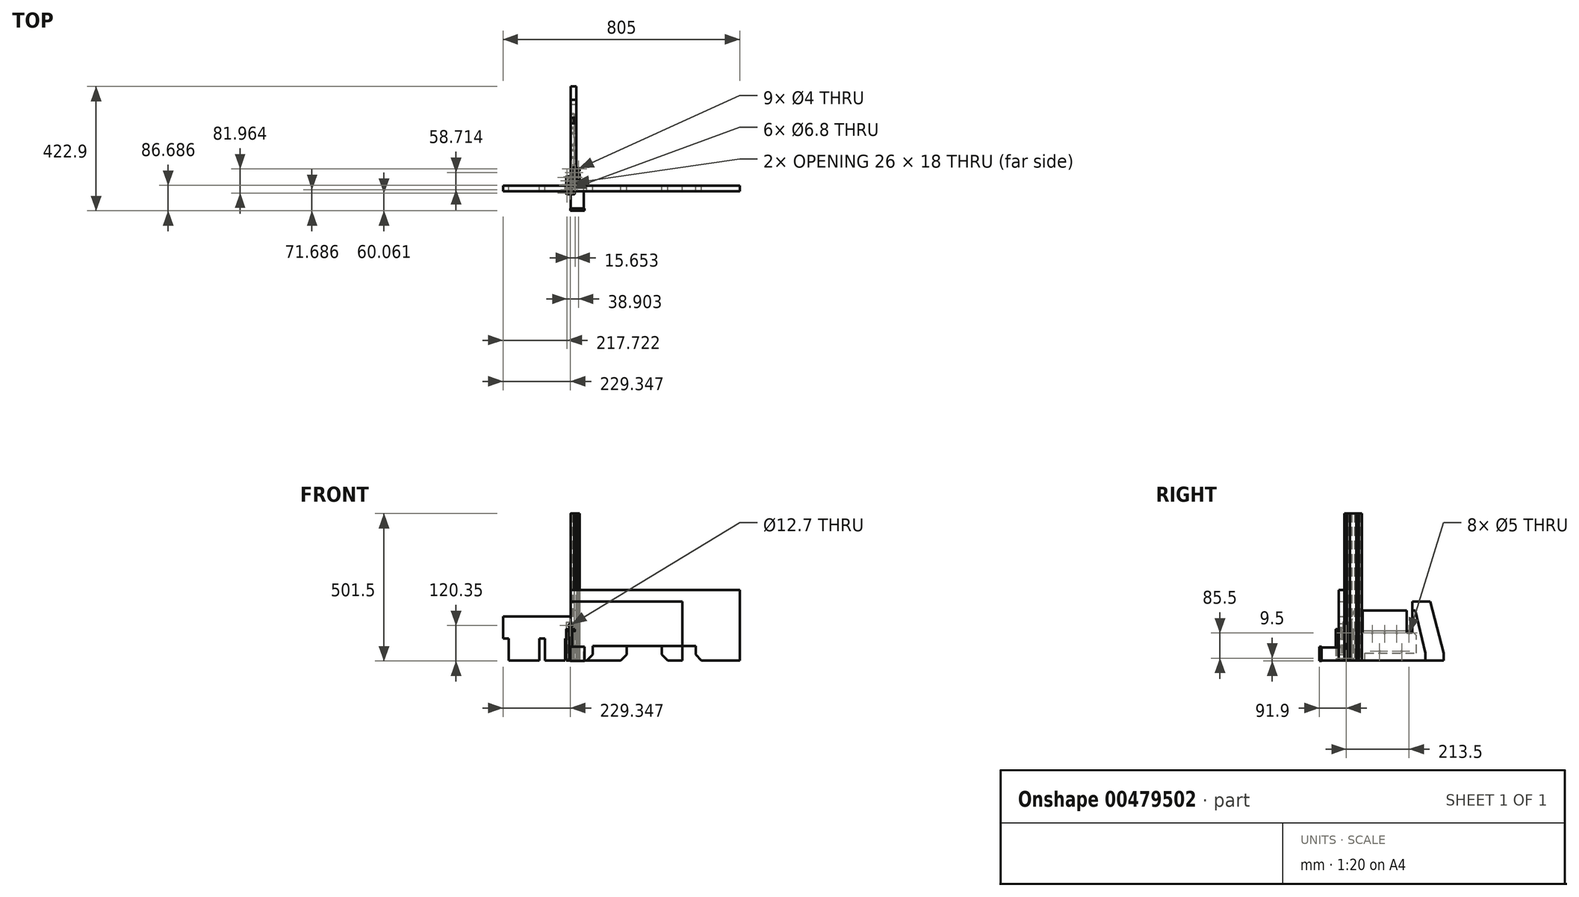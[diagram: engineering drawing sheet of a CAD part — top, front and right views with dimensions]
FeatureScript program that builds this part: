
annotation { "Feature Type Name" : "Feature", "Feature Type Description" : "" }
export const myFeature = defineFeature(function(context is Context, id is Id, definition is map)
    precondition{}
    {
        {
            var Q0;
            Q0=qCreatedBy(makeId("Top.planeOp"),FACE);
            var sketch = newSketch(context, id + "F0", { "sketchPlane" : qUnion([Q0])});
            skLineSegment(sketch, "E0.bottom", {"start": v(2, 60) * mm, "end": v(28, 60) * mm});
            skLineSegment(sketch, "E0.top", {"start": v(2, 0) * mm, "end": v(28, 0) * mm});
            skLineSegment(sketch, "E0.left", {"start": v(0, 58) * mm, "end": v(0, 2) * mm});
            skLineSegment(sketch, "E0.right", {"start": v(30, 58) * mm, "end": v(30, 2) * mm});
            skCircle(sketch, "E1", {"center": v(3.37, 56.62) * mm, "radius": 2 * mm});
            skCircle(sketch, "E2", {"center": v(26.62, 56.62) * mm, "radius": 2 * mm});
            skCircle(sketch, "E3", {"center": v(26.62, 3.38) * mm, "radius": 2 * mm});
            skCircle(sketch, "E4", {"center": v(3.37, 3.37) * mm, "radius": 2 * mm});
            skCircle(sketch, "E5", {"center": v(15, 45) * mm, "radius": 3.4 * mm});
            skCircle(sketch, "E6", {"center": v(15, 15) * mm, "radius": 3.4 * mm});
            skLineSegment(sketch, "E7", {"start": v(15, 60) * mm, "end": v(15, 0) * mm, "construction": true});
            skLineSegment(sketch, "E8.bottom", {"start": v(21, 39) * mm, "end": v(9, 39) * mm});
            skLineSegment(sketch, "E8.top", {"start": v(21, 51) * mm, "end": v(10.41, 51) * mm});
            skLineSegment(sketch, "E8.left", {"start": v(21, 39) * mm, "end": v(21, 51) * mm});
            skLineSegment(sketch, "E8.right", {"start": v(9, 39) * mm, "end": v(9, 49.59) * mm});
            skPoint(sketch, "E9.visualSharp", {"position": v(30, 60) * mm});
            skArc(sketch, "E9.filletArc", {"start": v(30, 58) * mm, "mid": v(29.41, 59.41) * mm, "end": v(28, 60) * mm});
            skPoint(sketch, "E10.visualSharp", {"position": v(0, 60) * mm});
            skArc(sketch, "E10.filletArc", {"start": v(2, 60) * mm, "mid": v(0.59, 59.41) * mm, "end": v(0, 58) * mm});
            skPoint(sketch, "E11.visualSharp", {"position": v(0, 0) * mm});
            skArc(sketch, "E11.filletArc", {"start": v(0, 2) * mm, "mid": v(0.59, 0.59) * mm, "end": v(2, 0) * mm});
            skPoint(sketch, "E12.visualSharp", {"position": v(30, 0) * mm});
            skArc(sketch, "E12.filletArc", {"start": v(28, 0) * mm, "mid": v(29.41, 0.59) * mm, "end": v(30, 2) * mm});
            skLineSegment(sketch, "E13.bottom", {"start": v(21, 9) * mm, "end": v(9, 9) * mm});
            skLineSegment(sketch, "E13.top", {"start": v(21, 21) * mm, "end": v(9, 21) * mm});
            skLineSegment(sketch, "E13.left", {"start": v(21, 9) * mm, "end": v(21, 21) * mm});
            skLineSegment(sketch, "E13.right", {"start": v(9, 9) * mm, "end": v(9, 21) * mm});
            skLineSegment(sketch, "E14", {"start": v(0, 49) * mm, "end": v(2, 49) * mm});
            skLineSegment(sketch, "E15", {"start": v(2, 49) * mm, "end": v(2, 53.38) * mm});
            skLineSegment(sketch, "E16", {"start": v(2, 53.37) * mm, "end": v(5.21, 53.37) * mm});
            skLineSegment(sketch, "E17", {"start": v(5.21, 53.38) * mm, "end": v(9, 49.59) * mm});
            skLineSegment(sketch, "E18", {"start": v(11, 60) * mm, "end": v(11, 58) * mm});
            skLineSegment(sketch, "E19", {"start": v(11, 58) * mm, "end": v(6.62, 58) * mm});
            skLineSegment(sketch, "E20", {"start": v(6.62, 58) * mm, "end": v(6.62, 54.79) * mm});
            skLineSegment(sketch, "E21", {"start": v(6.63, 54.79) * mm, "end": v(10.41, 51) * mm});
            skPoint(sketch, "E22.orphan", {"position": v(9, 51) * mm});
            skLineSegment(sketch, "E23", {"start": v(0, 30) * mm, "end": v(30, 30) * mm, "construction": true});
            skPoint(sketch, "E24.MirrorP", {"position": v(21, 51) * mm});
            skLineSegment(sketch, "E25.MirrorCS", {"start": v(30, 49) * mm, "end": v(28, 49) * mm});
            skLineSegment(sketch, "E26.MirrorCS", {"start": v(24.79, 53.38) * mm, "end": v(21, 49.59) * mm});
            skCircle(sketch, "E27.MirrorC", {"center": v(26.63, 56.62) * mm, "radius": 2 * mm});
            skLineSegment(sketch, "E28.MirrorCS", {"start": v(28, 49) * mm, "end": v(28, 53.38) * mm});
            skLineSegment(sketch, "E29.MirrorCS", {"start": v(19, 58) * mm, "end": v(23.38, 58) * mm});
            skLineSegment(sketch, "E30.MirrorCS", {"start": v(23.37, 54.79) * mm, "end": v(19.59, 51) * mm});
            skLineSegment(sketch, "E31.MirrorCS", {"start": v(19, 60) * mm, "end": v(19, 58) * mm});
            skLineSegment(sketch, "E32.MirrorCS", {"start": v(23.38, 58) * mm, "end": v(23.38, 54.79) * mm});
            skArc(sketch, "E33.MirrorCS", {"start": v(28, 60) * mm, "mid": v(29.41, 59.41) * mm, "end": v(30, 58) * mm});
            skLineSegment(sketch, "E34.MirrorCS", {"start": v(28, 53.37) * mm, "end": v(24.79, 53.37) * mm});
            skArc(sketch, "E35.MirrorCS", {"start": v(30, 2) * mm, "mid": v(29.41, 0.59) * mm, "end": v(28, 0) * mm});
            skCircle(sketch, "E36.MirrorC", {"center": v(26.62, 3.37) * mm, "radius": 2 * mm});
            skCircle(sketch, "E37.MirrorC", {"center": v(26.63, 3.38) * mm, "radius": 2 * mm});
            skLineSegment(sketch, "E38.MirrorCS", {"start": v(19, 0) * mm, "end": v(19, 2) * mm});
            skLineSegment(sketch, "E39.MirrorCS", {"start": v(28, 6.63) * mm, "end": v(24.79, 6.63) * mm});
            skLineSegment(sketch, "E40.MirrorCS", {"start": v(28, 11) * mm, "end": v(28, 6.62) * mm});
            skPoint(sketch, "E41.MirrorP", {"position": v(21, 9) * mm});
            skLineSegment(sketch, "E42.MirrorCS", {"start": v(23.37, 5.21) * mm, "end": v(19.59, 9) * mm});
            skLineSegment(sketch, "E43.MirrorCS", {"start": v(30, 11) * mm, "end": v(28, 11) * mm});
            skLineSegment(sketch, "E44.MirrorCS", {"start": v(19, 2) * mm, "end": v(23.38, 2) * mm});
            skLineSegment(sketch, "E45.MirrorCS", {"start": v(24.79, 6.62) * mm, "end": v(21, 10.41) * mm});
            skLineSegment(sketch, "E46.MirrorCS", {"start": v(23.38, 2) * mm, "end": v(23.38, 5.21) * mm});
            skLineSegment(sketch, "E47.MirrorCS", {"start": v(0, 11) * mm, "end": v(2, 11) * mm});
            skArc(sketch, "E48.MirrorCS", {"start": v(2, 0) * mm, "mid": v(0.59, 0.59) * mm, "end": v(0, 2) * mm});
            skLineSegment(sketch, "E49.MirrorCS", {"start": v(11, 0) * mm, "end": v(11, 2) * mm});
            skLineSegment(sketch, "E50.MirrorCS", {"start": v(2, 6.63) * mm, "end": v(5.21, 6.63) * mm});
            skLineSegment(sketch, "E51.MirrorCS", {"start": v(5.21, 6.62) * mm, "end": v(9, 10.41) * mm});
            skPoint(sketch, "E52.MirrorP", {"position": v(9, 9) * mm});
            skLineSegment(sketch, "E53.MirrorCS", {"start": v(6.63, 5.21) * mm, "end": v(10.41, 9) * mm});
            skCircle(sketch, "E54.MirrorC", {"center": v(3.37, 3.38) * mm, "radius": 2 * mm});
            skLineSegment(sketch, "E55.MirrorCS", {"start": v(11, 2) * mm, "end": v(6.62, 2) * mm});
            skLineSegment(sketch, "E56.MirrorCS", {"start": v(6.62, 2) * mm, "end": v(6.62, 5.21) * mm});
            skLineSegment(sketch, "E57.MirrorCS", {"start": v(2, 11) * mm, "end": v(2, 6.62) * mm});
            skLineSegment(sketch, "E58", {"start": v(9, 51) * mm, "end": v(10.41, 51) * mm});
            skLineSegment(sketch, "E59", {"start": v(9, 49.59) * mm, "end": v(9, 51) * mm});
            skLineSegment(sketch, "E60", {"start": v(0, 41) * mm, "end": v(2, 41) * mm});
            skLineSegment(sketch, "E61", {"start": v(2, 41) * mm, "end": v(2, 36.62) * mm});
            skLineSegment(sketch, "E62", {"start": v(2, 36.62) * mm, "end": v(5.21, 36.62) * mm});
            skLineSegment(sketch, "E63", {"start": v(5.21, 36.62) * mm, "end": v(9, 40.41) * mm});
            skLineSegment(sketch, "E64", {"start": v(10.41, 39) * mm, "end": v(6.04, 34.62) * mm});
            skLineSegment(sketch, "E65", {"start": v(6.04, 34.62) * mm, "end": v(2, 34.62) * mm});
            skLineSegment(sketch, "E66", {"start": v(2, 34.62) * mm, "end": v(2, 30) * mm});
            skLineSegment(sketch, "E67.MirrorCS", {"start": v(30, 41) * mm, "end": v(28, 41) * mm});
            skLineSegment(sketch, "E68.MirrorCS", {"start": v(28, 34.62) * mm, "end": v(28, 30) * mm});
            skLineSegment(sketch, "E69.MirrorCS", {"start": v(28, 41) * mm, "end": v(28, 36.62) * mm});
            skLineSegment(sketch, "E70.MirrorCS", {"start": v(19.59, 39) * mm, "end": v(23.96, 34.62) * mm});
            skLineSegment(sketch, "E71.MirrorCS", {"start": v(23.96, 34.62) * mm, "end": v(28, 34.62) * mm});
            skLineSegment(sketch, "E72.MirrorCS", {"start": v(28, 36.62) * mm, "end": v(24.79, 36.62) * mm});
            skLineSegment(sketch, "E73.MirrorCS", {"start": v(24.79, 36.62) * mm, "end": v(21, 40.41) * mm});
            skLineSegment(sketch, "E74.MirrorCS", {"start": v(28, 23.38) * mm, "end": v(24.79, 23.38) * mm});
            skLineSegment(sketch, "E75.MirrorCS", {"start": v(28, 25.38) * mm, "end": v(28, 30) * mm});
            skLineSegment(sketch, "E76.MirrorCS", {"start": v(19.59, 21) * mm, "end": v(23.96, 25.38) * mm});
            skLineSegment(sketch, "E77.MirrorCS", {"start": v(2, 19) * mm, "end": v(2, 23.38) * mm});
            skLineSegment(sketch, "E78.MirrorCS", {"start": v(28, 19) * mm, "end": v(28, 23.38) * mm});
            skLineSegment(sketch, "E79.MirrorCS", {"start": v(2, 25.38) * mm, "end": v(2, 30) * mm});
            skLineSegment(sketch, "E80.MirrorCS", {"start": v(10.41, 21) * mm, "end": v(6.04, 25.38) * mm});
            skLineSegment(sketch, "E81.MirrorCS", {"start": v(24.79, 23.38) * mm, "end": v(21, 19.59) * mm});
            skLineSegment(sketch, "E82.MirrorCS", {"start": v(2, 23.38) * mm, "end": v(5.21, 23.38) * mm});
            skLineSegment(sketch, "E83.MirrorCS", {"start": v(23.96, 25.38) * mm, "end": v(28, 25.38) * mm});
            skLineSegment(sketch, "E84.MirrorCS", {"start": v(5.21, 23.38) * mm, "end": v(9, 19.59) * mm});
            skLineSegment(sketch, "E85.MirrorCS", {"start": v(30, 19) * mm, "end": v(28, 19) * mm});
            skLineSegment(sketch, "E86.MirrorCS", {"start": v(6.04, 25.38) * mm, "end": v(2, 25.38) * mm});
            skLineSegment(sketch, "E87.MirrorCS", {"start": v(0, 19) * mm, "end": v(2, 19) * mm});
            skSolve(sketch);
        }
        {
            var Q0;
            Q0=makeQuery(id+"F0.imprint","IMPRINT",FACE,{"disambiguationData":[TD([[makeQuery(id+"F0.imprint","IMPRINT",EDGE,{"derivedFrom":sQuery(id+"F0.wireOp",EDGE,"E1")}),-1.0]])]});
            var Q1;
            {var subQ5=sQuery(id+"F0.wireOp",EDGE,"E25.MirrorCS");Q1=makeQuery(id+"F0.imprint","IMPRINT",FACE,{"disambiguationData":[TD([[makeQuery(id+"F0.imprint","IMPRINT",EDGE,{"derivedFrom":subQ5}),-1.0]])]});}
            var Q2;
            Q2=makeQuery(id+"F0.imprint","IMPRINT",FACE,{"disambiguationData":[TD([[makeQuery(id+"F0.imprint","IMPRINT",EDGE,{"derivedFrom":sQuery(id+"F0.wireOp",EDGE,"E5")}),-1.0]])]});
            var Q3;
            {var subQ4=sQuery(id+"F0.wireOp",EDGE,"E67.MirrorCS");Q3=makeQuery(id+"F0.imprint","IMPRINT",FACE,{"disambiguationData":[TD([[makeQuery(id+"F0.imprint","IMPRINT",EDGE,{"derivedFrom":subQ4}),1.0]])]});}
            var Q4;
            {var subQ6=sQuery(id+"F0.wireOp",EDGE,"E60");Q4=makeQuery(id+"F0.imprint","IMPRINT",FACE,{"disambiguationData":[TD([[makeQuery(id+"F0.imprint","IMPRINT",EDGE,{"derivedFrom":subQ6}),-1.0]])]});}
            var Q5;
            Q5=makeQuery(id+"F0.imprint","IMPRINT",FACE,{"disambiguationData":[TD([[makeQuery(id+"F0.imprint","IMPRINT",EDGE,{"derivedFrom":sQuery(id+"F0.wireOp",EDGE,"E6")}),-1.0]])]});
            var Q6;
            {var subQ5=sQuery(id+"F0.wireOp",EDGE,"E47.MirrorCS");Q6=makeQuery(id+"F0.imprint","IMPRINT",FACE,{"disambiguationData":[TD([[makeQuery(id+"F0.imprint","IMPRINT",EDGE,{"derivedFrom":subQ5}),-1.0]])]});}
            var Q7;
            {var subQ1=sQuery(id+"F0.wireOp",EDGE,"E12.filletArc");Q7=makeQuery(id+"F0.imprint","IMPRINT",FACE,{"disambiguationData":[TD([[makeQuery(id+"F0.imprint","IMPRINT",EDGE,{"derivedFrom":subQ1}),1.0]])]});}
            extrude(context, id + "F1", {"entities" : qUnion([Q0, Q1, Q2, Q3, Q4, Q5, Q6, Q7]), "depth" : 500 * mm});
        }
        {
            var Q0;
            Q0=qCreatedBy(makeId("Front.planeOp"),FACE);
            var sketch = newSketch(context, id + "F2", { "sketchPlane" : qUnion([Q0])});
            skLineSegment(sketch, "E88.bottom", {"start": v(0, 0) * mm, "end": v(-230, 0) * mm});
            skLineSegment(sketch, "E88.top", {"start": v(0, 150) * mm, "end": v(-230, 150) * mm});
            skLineSegment(sketch, "E88.left", {"start": v(0, 0) * mm, "end": v(0, 150) * mm});
            skLineSegment(sketch, "E88.right", {"start": v(-230, 0) * mm, "end": v(-230, 150) * mm});
            skLineSegment(sketch, "E89", {"start": v(-106, 75) * mm, "end": v(-106, 0) * mm});
            skLineSegment(sketch, "E90", {"start": v(-87, 75) * mm, "end": v(-87, 0) * mm});
            skLineSegment(sketch, "E91", {"start": v(-106, 75) * mm, "end": v(-87, 75) * mm});
            skLineSegment(sketch, "E92", {"start": v(-230, 75) * mm, "end": v(-211, 75) * mm});
            skLineSegment(sketch, "E93", {"start": v(-211, 75) * mm, "end": v(-211, 0) * mm});
            skLineSegment(sketch, "E94", {"start": v(0, 75) * mm, "end": v(-19, 75) * mm});
            skLineSegment(sketch, "E95", {"start": v(-19, 75) * mm, "end": v(-19, 0) * mm});
            skSolve(sketch);
        }
        {
            var Q0;
            {var subQ4=sQuery(id+"F2.wireOp",EDGE,"E88.top");Q0=makeQuery(id+"F2.imprint","IMPRINT",FACE,{"disambiguationData":[TD([[makeQuery(id+"F2.imprint","IMPRINT",EDGE,{"derivedFrom":subQ4}),1.0]])]});}
            extrude(context, id + "F3", {"entities" : qUnion([Q0]), "depth" : 19 * mm});
        }
        {
            var Q0;
            Q0=qCreatedBy(makeId("Right.planeOp"),FACE);
            var sketch = newSketch(context, id + "F4", { "sketchPlane" : qUnion([Q0])});
            skLineSegment(sketch, "E96", {"start": v(0, 0) * mm, "end": v(275, 0) * mm});
            skLineSegment(sketch, "E97", {"start": v(241.5, 170) * mm, "end": v(231.5, 170) * mm});
            skLineSegment(sketch, "E98", {"start": v(231.5, 170) * mm, "end": v(231.5, 95) * mm});
            skLineSegment(sketch, "E99", {"start": v(231.5, 95) * mm, "end": v(212.5, 95) * mm});
            skLineSegment(sketch, "E100", {"start": v(212.5, 95) * mm, "end": v(212.5, 170) * mm});
            skLineSegment(sketch, "E101", {"start": v(212.5, 170) * mm, "end": v(62.5, 170) * mm});
            skLineSegment(sketch, "E102", {"start": v(62.5, 170) * mm, "end": v(62.5, 95) * mm});
            skLineSegment(sketch, "E103", {"start": v(62.5, 95) * mm, "end": v(43.5, 95) * mm});
            skLineSegment(sketch, "E104", {"start": v(43.5, 95) * mm, "end": v(43.5, 170) * mm});
            skLineSegment(sketch, "E105", {"start": v(43.5, 170) * mm, "end": v(33.5, 170) * mm});
            skLineSegment(sketch, "E106", {"start": v(275, 0) * mm, "end": v(275, 25) * mm});
            skLineSegment(sketch, "E107", {"start": v(275, 25) * mm, "end": v(241.5, 170) * mm});
            skLineSegment(sketch, "E108", {"start": v(0, 0) * mm, "end": v(0, 25) * mm});
            skLineSegment(sketch, "E109", {"start": v(0, 25) * mm, "end": v(33.5, 170) * mm});
            skSolve(sketch);
        }
        {
            var Q0;
            Q0=makeQuery(id+"F4.imprint","IMPRINT",FACE,{"disambiguationData":[TD([[makeQuery(id+"F4.imprint","IMPRINT",EDGE,{"derivedFrom":sQuery(id+"F4.wireOp",EDGE,"E96")}),1.0]])]});
            extrude(context, id + "F5", {"entities" : qUnion([Q0]), "depth" : 19 * mm});
        }
        {
            var Q0;
            Q0=qCreatedBy(makeId("Top.planeOp"),FACE);
            var sketch = newSketch(context, id + "F6", { "sketchPlane" : qUnion([Q0])});
            skLineSegment(sketch, "E110.bottom", {"start": v(-13.65, 31.29) * mm, "end": v(12.35, 31.29) * mm});
            skLineSegment(sketch, "E110.top", {"start": v(-13.65, -28.71) * mm, "end": v(12.35, -28.71) * mm});
            skLineSegment(sketch, "E110.left", {"start": v(-15.65, 29.29) * mm, "end": v(-15.65, -26.71) * mm});
            skLineSegment(sketch, "E110.right", {"start": v(14.35, 29.29) * mm, "end": v(14.35, -26.71) * mm});
            skCircle(sketch, "E111", {"center": v(-12.28, 27.91) * mm, "radius": 2 * mm});
            skCircle(sketch, "E112", {"center": v(10.97, 27.91) * mm, "radius": 2 * mm});
            skCircle(sketch, "E113", {"center": v(10.97, -25.34) * mm, "radius": 2 * mm});
            skCircle(sketch, "E114", {"center": v(-12.28, -25.34) * mm, "radius": 2 * mm});
            skCircle(sketch, "E115", {"center": v(-0.65, 16.29) * mm, "radius": 3.4 * mm});
            skCircle(sketch, "E116", {"center": v(-0.65, -13.71) * mm, "radius": 3.4 * mm});
            skLineSegment(sketch, "E117", {"start": v(-0.65, 31.29) * mm, "end": v(-0.65, -28.71) * mm, "construction": true});
            skLineSegment(sketch, "E118.bottom", {"start": v(5.35, 10.29) * mm, "end": v(-6.65, 10.29) * mm});
            skLineSegment(sketch, "E118.top", {"start": v(5.35, 22.29) * mm, "end": v(-5.24, 22.29) * mm});
            skLineSegment(sketch, "E118.left", {"start": v(5.35, 10.29) * mm, "end": v(5.35, 22.29) * mm});
            skLineSegment(sketch, "E118.right", {"start": v(-6.65, 10.29) * mm, "end": v(-6.65, 20.87) * mm});
            skPoint(sketch, "E119.visualSharp", {"position": v(14.35, 31.29) * mm});
            skArc(sketch, "E119.filletArc", {"start": v(14.35, 29.29) * mm, "mid": v(13.76, 30.7) * mm, "end": v(12.35, 31.29) * mm});
            skPoint(sketch, "E120.visualSharp", {"position": v(-15.65, 31.29) * mm});
            skArc(sketch, "E120.filletArc", {"start": v(-13.65, 31.29) * mm, "mid": v(-15.07, 30.7) * mm, "end": v(-15.65, 29.29) * mm});
            skPoint(sketch, "E121.visualSharp", {"position": v(-15.65, -28.71) * mm});
            skArc(sketch, "E121.filletArc", {"start": v(-15.65, -26.71) * mm, "mid": v(-15.07, -28.13) * mm, "end": v(-13.65, -28.71) * mm});
            skPoint(sketch, "E122.visualSharp", {"position": v(14.35, -28.71) * mm});
            skArc(sketch, "E122.filletArc", {"start": v(12.35, -28.71) * mm, "mid": v(13.76, -28.13) * mm, "end": v(14.35, -26.71) * mm});
            skLineSegment(sketch, "E123.bottom", {"start": v(5.35, -19.71) * mm, "end": v(-6.65, -19.71) * mm});
            skLineSegment(sketch, "E123.top", {"start": v(5.35, -7.71) * mm, "end": v(-6.65, -7.71) * mm});
            skLineSegment(sketch, "E123.left", {"start": v(5.35, -19.71) * mm, "end": v(5.35, -7.71) * mm});
            skLineSegment(sketch, "E123.right", {"start": v(-6.65, -19.71) * mm, "end": v(-6.65, -7.71) * mm});
            skLineSegment(sketch, "E124", {"start": v(-15.65, 20.29) * mm, "end": v(-13.65, 20.29) * mm});
            skLineSegment(sketch, "E125", {"start": v(-13.65, 20.29) * mm, "end": v(-13.65, 24.66) * mm});
            skLineSegment(sketch, "E126", {"start": v(-13.65, 24.66) * mm, "end": v(-10.44, 24.66) * mm});
            skLineSegment(sketch, "E127", {"start": v(-10.44, 24.66) * mm, "end": v(-6.65, 20.87) * mm});
            skLineSegment(sketch, "E128", {"start": v(-4.65, 31.29) * mm, "end": v(-4.65, 29.29) * mm});
            skLineSegment(sketch, "E129", {"start": v(-4.65, 29.29) * mm, "end": v(-9.03, 29.29) * mm});
            skLineSegment(sketch, "E130", {"start": v(-9.03, 29.29) * mm, "end": v(-9.03, 26.08) * mm});
            skLineSegment(sketch, "E131", {"start": v(-9.03, 26.08) * mm, "end": v(-5.24, 22.29) * mm});
            skPoint(sketch, "E132.orphan", {"position": v(-6.65, 22.29) * mm});
            skLineSegment(sketch, "E133", {"start": v(-15.65, 1.29) * mm, "end": v(14.35, 1.29) * mm, "construction": true});
            skPoint(sketch, "E134.MirrorP", {"position": v(5.35, 22.29) * mm});
            skLineSegment(sketch, "E135.MirrorCS", {"start": v(14.35, 20.29) * mm, "end": v(12.35, 20.29) * mm});
            skLineSegment(sketch, "E136.MirrorCS", {"start": v(9.14, 24.66) * mm, "end": v(5.35, 20.87) * mm});
            skLineSegment(sketch, "E137.MirrorCS", {"start": v(12.35, 20.29) * mm, "end": v(12.35, 24.66) * mm});
            skLineSegment(sketch, "E138.MirrorCS", {"start": v(3.35, 29.29) * mm, "end": v(7.72, 29.29) * mm});
            skLineSegment(sketch, "E139.MirrorCS", {"start": v(7.72, 26.08) * mm, "end": v(3.93, 22.29) * mm});
            skLineSegment(sketch, "E140.MirrorCS", {"start": v(3.35, 31.29) * mm, "end": v(3.35, 29.29) * mm});
            skLineSegment(sketch, "E141.MirrorCS", {"start": v(7.72, 29.29) * mm, "end": v(7.72, 26.08) * mm});
            skArc(sketch, "E142.MirrorCS", {"start": v(12.35, 31.29) * mm, "mid": v(13.76, 30.7) * mm, "end": v(14.35, 29.29) * mm});
            skLineSegment(sketch, "E143.MirrorCS", {"start": v(12.35, 24.66) * mm, "end": v(9.14, 24.66) * mm});
            skArc(sketch, "E144.MirrorCS", {"start": v(14.35, -26.71) * mm, "mid": v(13.76, -28.13) * mm, "end": v(12.35, -28.71) * mm});
            skLineSegment(sketch, "E145.MirrorCS", {"start": v(3.35, -28.71) * mm, "end": v(3.35, -26.71) * mm});
            skLineSegment(sketch, "E146.MirrorCS", {"start": v(12.35, -22.09) * mm, "end": v(9.14, -22.09) * mm});
            skLineSegment(sketch, "E147.MirrorCS", {"start": v(12.35, -17.71) * mm, "end": v(12.35, -22.09) * mm});
            skPoint(sketch, "E148.MirrorP", {"position": v(5.35, -19.71) * mm});
            skLineSegment(sketch, "E149.MirrorCS", {"start": v(7.72, -23.5) * mm, "end": v(3.93, -19.71) * mm});
            skLineSegment(sketch, "E150.MirrorCS", {"start": v(14.35, -17.71) * mm, "end": v(12.35, -17.71) * mm});
            skLineSegment(sketch, "E151.MirrorCS", {"start": v(3.35, -26.71) * mm, "end": v(7.72, -26.71) * mm});
            skLineSegment(sketch, "E152.MirrorCS", {"start": v(9.14, -22.09) * mm, "end": v(5.35, -18.3) * mm});
            skLineSegment(sketch, "E153.MirrorCS", {"start": v(7.72, -26.71) * mm, "end": v(7.72, -23.5) * mm});
            skLineSegment(sketch, "E154.MirrorCS", {"start": v(-15.65, -17.71) * mm, "end": v(-13.65, -17.71) * mm});
            skArc(sketch, "E155.MirrorCS", {"start": v(-13.65, -28.71) * mm, "mid": v(-15.07, -28.13) * mm, "end": v(-15.65, -26.71) * mm});
            skLineSegment(sketch, "E156.MirrorCS", {"start": v(-4.65, -28.71) * mm, "end": v(-4.65, -26.71) * mm});
            skLineSegment(sketch, "E157.MirrorCS", {"start": v(-13.65, -22.09) * mm, "end": v(-10.44, -22.09) * mm});
            skLineSegment(sketch, "E158.MirrorCS", {"start": v(-10.44, -22.09) * mm, "end": v(-6.65, -18.3) * mm});
            skPoint(sketch, "E159.MirrorP", {"position": v(-6.65, -19.71) * mm});
            skLineSegment(sketch, "E160.MirrorCS", {"start": v(-9.03, -23.5) * mm, "end": v(-5.24, -19.71) * mm});
            skLineSegment(sketch, "E161.MirrorCS", {"start": v(-4.65, -26.71) * mm, "end": v(-9.03, -26.71) * mm});
            skLineSegment(sketch, "E162.MirrorCS", {"start": v(-9.03, -26.71) * mm, "end": v(-9.03, -23.5) * mm});
            skLineSegment(sketch, "E163.MirrorCS", {"start": v(-13.65, -17.71) * mm, "end": v(-13.65, -22.09) * mm});
            skLineSegment(sketch, "E164", {"start": v(-6.65, 22.29) * mm, "end": v(-5.24, 22.29) * mm});
            skLineSegment(sketch, "E165", {"start": v(-6.65, 20.87) * mm, "end": v(-6.65, 22.29) * mm});
            skLineSegment(sketch, "E166", {"start": v(-15.65, 12.29) * mm, "end": v(-13.65, 12.29) * mm});
            skLineSegment(sketch, "E167", {"start": v(-13.65, 12.29) * mm, "end": v(-13.65, 7.91) * mm});
            skLineSegment(sketch, "E168", {"start": v(-13.65, 7.91) * mm, "end": v(-10.44, 7.91) * mm});
            skLineSegment(sketch, "E169", {"start": v(-10.44, 7.91) * mm, "end": v(-6.65, 11.7) * mm});
            skLineSegment(sketch, "E170", {"start": v(-5.24, 10.29) * mm, "end": v(-9.61, 5.91) * mm});
            skLineSegment(sketch, "E171", {"start": v(-9.61, 5.91) * mm, "end": v(-13.65, 5.91) * mm});
            skLineSegment(sketch, "E172", {"start": v(-13.65, 5.91) * mm, "end": v(-13.65, 1.29) * mm});
            skLineSegment(sketch, "E173.MirrorCS", {"start": v(14.35, 12.29) * mm, "end": v(12.35, 12.29) * mm});
            skLineSegment(sketch, "E174.MirrorCS", {"start": v(12.35, 5.91) * mm, "end": v(12.35, 1.29) * mm});
            skLineSegment(sketch, "E175.MirrorCS", {"start": v(12.35, 12.29) * mm, "end": v(12.35, 7.91) * mm});
            skLineSegment(sketch, "E176.MirrorCS", {"start": v(3.93, 10.29) * mm, "end": v(8.3, 5.91) * mm});
            skLineSegment(sketch, "E177.MirrorCS", {"start": v(8.3, 5.91) * mm, "end": v(12.35, 5.91) * mm});
            skLineSegment(sketch, "E178.MirrorCS", {"start": v(12.35, 7.91) * mm, "end": v(9.14, 7.91) * mm});
            skLineSegment(sketch, "E179.MirrorCS", {"start": v(9.14, 7.91) * mm, "end": v(5.35, 11.7) * mm});
            skLineSegment(sketch, "E180.MirrorCS", {"start": v(12.35, -5.34) * mm, "end": v(9.14, -5.34) * mm});
            skLineSegment(sketch, "E181.MirrorCS", {"start": v(12.35, -3.34) * mm, "end": v(12.35, 1.29) * mm});
            skLineSegment(sketch, "E182.MirrorCS", {"start": v(3.93, -7.71) * mm, "end": v(8.3, -3.34) * mm});
            skLineSegment(sketch, "E183.MirrorCS", {"start": v(-13.65, -9.71) * mm, "end": v(-13.65, -5.34) * mm});
            skLineSegment(sketch, "E184.MirrorCS", {"start": v(12.35, -9.71) * mm, "end": v(12.35, -5.34) * mm});
            skLineSegment(sketch, "E185.MirrorCS", {"start": v(-13.65, -3.34) * mm, "end": v(-13.65, 1.29) * mm});
            skLineSegment(sketch, "E186.MirrorCS", {"start": v(-5.24, -7.71) * mm, "end": v(-9.61, -3.34) * mm});
            skLineSegment(sketch, "E187.MirrorCS", {"start": v(9.14, -5.34) * mm, "end": v(5.35, -9.13) * mm});
            skLineSegment(sketch, "E188.MirrorCS", {"start": v(-13.65, -5.34) * mm, "end": v(-10.44, -5.34) * mm});
            skLineSegment(sketch, "E189.MirrorCS", {"start": v(8.3, -3.34) * mm, "end": v(12.35, -3.34) * mm});
            skLineSegment(sketch, "E190.MirrorCS", {"start": v(-10.44, -5.34) * mm, "end": v(-6.65, -9.13) * mm});
            skLineSegment(sketch, "E191.MirrorCS", {"start": v(14.35, -9.71) * mm, "end": v(12.35, -9.71) * mm});
            skLineSegment(sketch, "E192.MirrorCS", {"start": v(-9.61, -3.34) * mm, "end": v(-13.65, -3.34) * mm});
            skLineSegment(sketch, "E193.MirrorCS", {"start": v(-15.65, -9.71) * mm, "end": v(-13.65, -9.71) * mm});
            skSolve(sketch);
        }
        {
            var Q0;
            Q0=makeQuery(id+"F6.imprint","IMPRINT",FACE,{"disambiguationData":[TD([[makeQuery(id+"F6.imprint","IMPRINT",EDGE,{"derivedFrom":sQuery(id+"F6.wireOp",EDGE,"E111")}),-1.0]])]});
            var Q1;
            Q1=makeQuery(id+"F6.imprint","IMPRINT",FACE,{"disambiguationData":[TD([[makeQuery(id+"F6.imprint","IMPRINT",EDGE,{"derivedFrom":sQuery(id+"F6.wireOp",EDGE,"E115")}),-1.0]])]});
            var Q2;
            {var subQ5=sQuery(id+"F6.wireOp",EDGE,"E135.MirrorCS");Q2=makeQuery(id+"F6.imprint","IMPRINT",FACE,{"disambiguationData":[TD([[makeQuery(id+"F6.imprint","IMPRINT",EDGE,{"derivedFrom":subQ5}),-1.0]])]});}
            var Q3;
            {var subQ4=sQuery(id+"F6.wireOp",EDGE,"E173.MirrorCS");Q3=makeQuery(id+"F6.imprint","IMPRINT",FACE,{"disambiguationData":[TD([[makeQuery(id+"F6.imprint","IMPRINT",EDGE,{"derivedFrom":subQ4}),1.0]])]});}
            var Q4;
            {var subQ6=sQuery(id+"F6.wireOp",EDGE,"E166");Q4=makeQuery(id+"F6.imprint","IMPRINT",FACE,{"disambiguationData":[TD([[makeQuery(id+"F6.imprint","IMPRINT",EDGE,{"derivedFrom":subQ6}),-1.0]])]});}
            var Q5;
            Q5=makeQuery(id+"F6.imprint","IMPRINT",FACE,{"disambiguationData":[TD([[makeQuery(id+"F6.imprint","IMPRINT",EDGE,{"derivedFrom":sQuery(id+"F6.wireOp",EDGE,"E116")}),-1.0]])]});
            var Q6;
            {var subQ5=sQuery(id+"F6.wireOp",EDGE,"E154.MirrorCS");Q6=makeQuery(id+"F6.imprint","IMPRINT",FACE,{"disambiguationData":[TD([[makeQuery(id+"F6.imprint","IMPRINT",EDGE,{"derivedFrom":subQ5}),-1.0]])]});}
            var Q7;
            {var subQ1=sQuery(id+"F6.wireOp",EDGE,"E122.filletArc");Q7=makeQuery(id+"F6.imprint","IMPRINT",FACE,{"disambiguationData":[TD([[makeQuery(id+"F6.imprint","IMPRINT",EDGE,{"derivedFrom":subQ1}),1.0]])]});}
            extrude(context, id + "F7", {"entities" : qUnion([Q0, Q1, Q2, Q3, Q4, Q5, Q6, Q7]), "depth" : 100 * mm});
        }
        {
            var Q0;
            Q0=qCreatedBy(makeId("Right.planeOp"),FACE);
            var sketch = newSketch(context, id + "F8", { "sketchPlane" : qUnion([Q0])});
            skLineSegment(sketch, "E194", {"start": v(0, 0) * mm, "end": v(337.5, 0) * mm});
            skLineSegment(sketch, "E195", {"start": v(291.5, 200) * mm, "end": v(231.5, 200) * mm});
            skLineSegment(sketch, "E196", {"start": v(231.5, 200) * mm, "end": v(231.5, 95) * mm});
            skLineSegment(sketch, "E197", {"start": v(231.5, 95) * mm, "end": v(212.5, 95) * mm});
            skLineSegment(sketch, "E198", {"start": v(212.5, 95) * mm, "end": v(212.5, 170) * mm});
            skLineSegment(sketch, "E199", {"start": v(212.5, 170) * mm, "end": v(62.5, 170) * mm});
            skLineSegment(sketch, "E200", {"start": v(62.5, 170) * mm, "end": v(62.5, 95) * mm});
            skLineSegment(sketch, "E201", {"start": v(62.5, 95) * mm, "end": v(43.5, 95) * mm});
            skLineSegment(sketch, "E202", {"start": v(43.5, 95) * mm, "end": v(43.5, 170) * mm});
            skLineSegment(sketch, "E203", {"start": v(337.5, 0) * mm, "end": v(337.5, 25) * mm});
            skLineSegment(sketch, "E204", {"start": v(337.5, 25) * mm, "end": v(291.5, 200) * mm});
            skLineSegment(sketch, "E205", {"start": v(0, 0) * mm, "end": v(0, 25) * mm});
            skLineSegment(sketch, "E206", {"start": v(0, 25) * mm, "end": v(33.5, 170) * mm});
            skLineSegment(sketch, "E207", {"start": v(33.5, 170) * mm, "end": v(43.5, 170) * mm});
            skLineSegment(sketch, "E208", {"start": v(137.5, 170) * mm, "end": v(137.5, 0) * mm, "construction": true});
            skSolve(sketch);
        }
        {
            var Q0;
            Q0 = qSketchRegion(id + "F8", true);
            extrude(context, id + "F9", {"entities" : qUnion([Q0]), "depth" : 19 * mm});
        }
        {
            var Q0;
            Q0=qCreatedBy(makeId("Front.planeOp"),FACE);
            var sketch = newSketch(context, id + "F10", { "sketchPlane" : qUnion([Q0])});
            skLineSegment(sketch, "E209", {"start": v(0, 0) * mm, "end": v(0, 240) * mm});
            skLineSegment(sketch, "E210", {"start": v(0, 240) * mm, "end": v(575, 240) * mm});
            skLineSegment(sketch, "E211", {"start": v(575, 240) * mm, "end": v(575, 0) * mm});
            skLineSegment(sketch, "E212", {"start": v(575, 0) * mm, "end": v(445, 0) * mm});
            skLineSegment(sketch, "E213", {"start": v(445, 0) * mm, "end": v(425, 20) * mm});
            skLineSegment(sketch, "E214", {"start": v(425, 20) * mm, "end": v(425, 50) * mm});
            skLineSegment(sketch, "E215", {"start": v(425, 50) * mm, "end": v(190, 50) * mm});
            skLineSegment(sketch, "E216", {"start": v(190, 50) * mm, "end": v(190, 20) * mm});
            skLineSegment(sketch, "E217", {"start": v(190, 20) * mm, "end": v(170, 0) * mm});
            skLineSegment(sketch, "E218", {"start": v(170, 0) * mm, "end": v(0, 0) * mm});
            skSolve(sketch);
        }
        {
            var Q0;
            Q0 = qSketchRegion(id + "F10", true);
            extrude(context, id + "F11", {"entities" : qUnion([Q0]), "depth" : 19 * mm, "offsetDistance" : 25 * mm});
        }
        {
            var Q0;
            Q0=qCreatedBy(makeId("Front.planeOp"),FACE);
            var sketch = newSketch(context, id + "F12", { "sketchPlane" : qUnion([Q0])});
            skLineSegment(sketch, "E219.bottom", {"start": v(0, 0) * mm, "end": v(45, 0) * mm});
            skLineSegment(sketch, "E219.top", {"start": v(0, 45) * mm, "end": v(45, 45) * mm});
            skLineSegment(sketch, "E219.left", {"start": v(0, 0) * mm, "end": v(0, 45) * mm});
            skLineSegment(sketch, "E219.right", {"start": v(45, 0) * mm, "end": v(45, 45) * mm});
            skSolve(sketch);
        }
        {
            var Q0;
            Q0=makeQuery(id+"F12.imprint","IMPRINT",FACE,{"disambiguationData":[TD([[makeQuery(id+"F12.imprint","IMPRINT",EDGE,{"derivedFrom":sQuery(id+"F12.wireOp",EDGE,"E219.bottom")}),1.0]])]});
            extrude(context, id + "F13", {"entities" : qUnion([Q0]), "depth" : 77 * mm, "offsetDistance" : 25 * mm});
        }
        {
            var Q0;
            Q0=makeQuery(id+"F13.opExtrude","CAP_FACE",FACE,{"disambiguationData":[OSD([sQuery(id+"F12.wireOp",EDGE,"E219.bottom"),sQuery(id+"F12.wireOp",EDGE,"E219.top"),sQuery(id+"F12.wireOp",EDGE,"E219.left"),sQuery(id+"F12.wireOp",EDGE,"E219.right")])],"isStart":false});
            var sketch = newSketch(context, id + "F14", { "sketchPlane" : qUnion([Q0])});
            skLineSegment(sketch, "E220", {"start": v(22.5, 45) * mm, "end": v(22.5, 0) * mm, "construction": true});
            skLineSegment(sketch, "E221.bottom", {"start": v(46.5, -1.5) * mm, "end": v(-1.5, -1.5) * mm});
            skLineSegment(sketch, "E221.top", {"start": v(46.5, 46.5) * mm, "end": v(-1.5, 46.5) * mm});
            skLineSegment(sketch, "E221.left", {"start": v(46.5, -1.5) * mm, "end": v(46.5, 46.5) * mm});
            skLineSegment(sketch, "E221.right", {"start": v(-1.5, -1.5) * mm, "end": v(-1.5, 46.5) * mm});
            skPoint(sketch, "E221.middle", {"position": v(22.5, 22.5) * mm});
            skSolve(sketch);
        }
        {
            var Q0;
            Q0=makeQuery(id+"F14.imprint","IMPRINT",FACE,{"disambiguationData":[TD([[makeQuery(id+"F14.imprint","IMPRINT",EDGE,{"derivedFrom":sQuery(id+"F14.wireOp",EDGE,"E221.bottom")}),-1.0]])]});
            var Q1;
            Q1=makeQuery(id+"F14.imprint","IMPRINT",FACE,{"disambiguationData":[TD([[makeQuery(id+"F14.imprint","IMPRINT",EDGE,{"derivedFrom":makeQuery(id+"F13.opExtrude","CAP_EDGE",EDGE,{"disambiguationData":[OSD([sQuery(id+"F12.wireOp",EDGE,"E219.bottom")])],"isStart":false})}),1.0]])]});
            extrude(context, id + "F15", {"entities" : qUnion([Q0, Q1]), "operationType" : NewBodyOperationType.ADD, "depth" : 8.4 * mm, "offsetDistance" : 25 * mm});
        }
        {
            var Q0;
            Q0=qCreatedBy(makeId("Right.planeOp"),FACE);
            var sketch = newSketch(context, id + "F16", { "sketchPlane" : qUnion([Q0])});
            skLineSegment(sketch, "E222.bottom", {"start": v(0, 0) * mm, "end": v(47.6, 0) * mm});
            skLineSegment(sketch, "E222.top", {"start": v(0, 35) * mm, "end": v(47.6, 35) * mm});
            skLineSegment(sketch, "E222.left", {"start": v(0, 0) * mm, "end": v(0, 35) * mm});
            skLineSegment(sketch, "E222.right", {"start": v(47.6, 0) * mm, "end": v(47.6, 35) * mm});
            skSolve(sketch);
        }
        {
            var Q0;
            Q0=makeQuery(id+"F16.imprint","IMPRINT",FACE,{"disambiguationData":[TD([[makeQuery(id+"F16.imprint","IMPRINT",EDGE,{"derivedFrom":sQuery(id+"F16.wireOp",EDGE,"E222.bottom")}),1.0]])]});
            extrude(context, id + "F17", {"entities" : qUnion([Q0]), "depth" : 19 * mm, "offsetDistance" : 25 * mm});
        }
        {
            var Q0;
            Q0=qCreatedBy(makeId("Front.planeOp"),FACE);
            var sketch = newSketch(context, id + "F18", { "sketchPlane" : qUnion([Q0])});
            skLineSegment(sketch, "E223", {"start": v(0, 0) * mm, "end": v(0, 200) * mm});
            skLineSegment(sketch, "E224", {"start": v(0, 200) * mm, "end": v(380, 200) * mm});
            skLineSegment(sketch, "E225", {"start": v(380, 200) * mm, "end": v(380, 0) * mm});
            skLineSegment(sketch, "E226", {"start": v(380, 0) * mm, "end": v(330, 0) * mm});
            skLineSegment(sketch, "E227", {"start": v(330, 0) * mm, "end": v(310, 20) * mm});
            skLineSegment(sketch, "E228", {"start": v(310, 20) * mm, "end": v(310, 50) * mm});
            skLineSegment(sketch, "E229", {"start": v(310, 50) * mm, "end": v(75, 50) * mm});
            skLineSegment(sketch, "E230", {"start": v(75, 50) * mm, "end": v(75, 20) * mm});
            skLineSegment(sketch, "E231", {"start": v(75, 20) * mm, "end": v(55, 0) * mm});
            skLineSegment(sketch, "E232", {"start": v(55, 0) * mm, "end": v(0, 0) * mm});
            skSolve(sketch);
        }
        {
            var Q0;
            Q0=makeQuery(id+"F18.imprint","IMPRINT",FACE,{"disambiguationData":[TD([[makeQuery(id+"F18.imprint","IMPRINT",EDGE,{"derivedFrom":sQuery(id+"F18.wireOp",EDGE,"E223")}),-1.0]])]});
            extrude(context, id + "F19", {"entities" : qUnion([Q0]), "depth" : 19 * mm, "offsetDistance" : 25 * mm});
        }
        {
            var Q0;
            Q0=qCreatedBy(makeId("Right.planeOp"),FACE);
            var sketch = newSketch(context, id + "F20", { "sketchPlane" : qUnion([Q0])});
            skLineSegment(sketch, "E233", {"start": v(0, 0) * mm, "end": v(70, 0) * mm});
            skLineSegment(sketch, "E234", {"start": v(70, 0) * mm, "end": v(70, 25) * mm});
            skLineSegment(sketch, "E235", {"start": v(70, 25) * mm, "end": v(245, 25) * mm});
            skLineSegment(sketch, "E236", {"start": v(245, 25) * mm, "end": v(245, 85) * mm});
            skLineSegment(sketch, "E237", {"start": v(245, 85) * mm, "end": v(230, 100) * mm});
            skLineSegment(sketch, "E238", {"start": v(230, 100) * mm, "end": v(0, 100) * mm});
            skLineSegment(sketch, "E239", {"start": v(0, 100) * mm, "end": v(0, 0) * mm});
            skCircle(sketch, "E240", {"center": v(6.5, 93.5) * mm, "radius": 2.5 * mm});
            skCircle(sketch, "E241", {"center": v(6.5, 8) * mm, "radius": 2.5 * mm});
            skCircle(sketch, "E242", {"center": v(120, 31.5) * mm, "radius": 2.5 * mm});
            skCircle(sketch, "E243", {"center": v(195, 31.5) * mm, "radius": 2.5 * mm});
            skCircle(sketch, "E244", {"center": v(220, 93.5) * mm, "radius": 2.5 * mm});
            skCircle(sketch, "E245", {"center": v(178, 93.5) * mm, "radius": 2.5 * mm});
            skCircle(sketch, "E246", {"center": v(137, 93.5) * mm, "radius": 2.5 * mm});
            skCircle(sketch, "E247", {"center": v(95, 93.5) * mm, "radius": 2.5 * mm});
            skSolve(sketch);
        }
        {
            var Q0;
            Q0=makeQuery(id+"F20.imprint","IMPRINT",FACE,{"disambiguationData":[TD([[makeQuery(id+"F20.imprint","IMPRINT",EDGE,{"derivedFrom":sQuery(id+"F20.wireOp",EDGE,"E233")}),1.0]])]});
            extrude(context, id + "F21", {"entities" : qUnion([Q0]), "depth" : 11 * mm, "offsetDistance" : 25 * mm});
        }
        {
            var Q0;
            Q0=makeQuery(id+"F7.opExtrude","CAP_FACE",FACE,{"disambiguationData":[OSD([sQuery(id+"F6.wireOp",EDGE,"E110.bottom"),sQuery(id+"F6.wireOp",EDGE,"E110.top"),sQuery(id+"F6.wireOp",EDGE,"E110.left"),sQuery(id+"F6.wireOp",EDGE,"E110.right"),sQuery(id+"F6.wireOp",EDGE,"E111"),sQuery(id+"F6.wireOp",EDGE,"E115"),sQuery(id+"F6.wireOp",EDGE,"E116"),sQuery(id+"F6.wireOp",EDGE,"E118.bottom"),sQuery(id+"F6.wireOp",EDGE,"E118.top"),sQuery(id+"F6.wireOp",EDGE,"E118.left"),sQuery(id+"F6.wireOp",EDGE,"E118.right"),sQuery(id+"F6.wireOp",EDGE,"E120.filletArc"),sQuery(id+"F6.wireOp",EDGE,"E123.bottom"),sQuery(id+"F6.wireOp",EDGE,"E123.left"),sQuery(id+"F6.wireOp",EDGE,"E123.right"),sQuery(id+"F6.wireOp",EDGE,"E124"),sQuery(id+"F6.wireOp",EDGE,"E125"),sQuery(id+"F6.wireOp",EDGE,"E126"),sQuery(id+"F6.wireOp",EDGE,"E127"),sQuery(id+"F6.wireOp",EDGE,"E128"),sQuery(id+"F6.wireOp",EDGE,"E129"),sQuery(id+"F6.wireOp",EDGE,"E130"),sQuery(id+"F6.wireOp",EDGE,"E131"),sQuery(id+"F6.wireOp",EDGE,"E135.MirrorCS"),sQuery(id+"F6.wireOp",EDGE,"E136.MirrorCS"),sQuery(id+"F6.wireOp",EDGE,"E112"),sQuery(id+"F6.wireOp",EDGE,"E137.MirrorCS"),sQuery(id+"F6.wireOp",EDGE,"E138.MirrorCS"),sQuery(id+"F6.wireOp",EDGE,"E139.MirrorCS"),sQuery(id+"F6.wireOp",EDGE,"E140.MirrorCS"),sQuery(id+"F6.wireOp",EDGE,"E141.MirrorCS"),sQuery(id+"F6.wireOp",EDGE,"E142.MirrorCS"),sQuery(id+"F6.wireOp",EDGE,"E143.MirrorCS"),sQuery(id+"F6.wireOp",EDGE,"E122.filletArc"),sQuery(id+"F6.wireOp",EDGE,"E113"),sQuery(id+"F6.wireOp",EDGE,"E145.MirrorCS"),sQuery(id+"F6.wireOp",EDGE,"E146.MirrorCS"),sQuery(id+"F6.wireOp",EDGE,"E147.MirrorCS"),sQuery(id+"F6.wireOp",EDGE,"E149.MirrorCS"),sQuery(id+"F6.wireOp",EDGE,"E150.MirrorCS"),sQuery(id+"F6.wireOp",EDGE,"E151.MirrorCS"),sQuery(id+"F6.wireOp",EDGE,"E152.MirrorCS"),sQuery(id+"F6.wireOp",EDGE,"E153.MirrorCS"),sQuery(id+"F6.wireOp",EDGE,"E154.MirrorCS"),sQuery(id+"F6.wireOp",EDGE,"E155.MirrorCS"),sQuery(id+"F6.wireOp",EDGE,"E156.MirrorCS"),sQuery(id+"F6.wireOp",EDGE,"E157.MirrorCS"),sQuery(id+"F6.wireOp",EDGE,"E158.MirrorCS"),sQuery(id+"F6.wireOp",EDGE,"E160.MirrorCS"),sQuery(id+"F6.wireOp",EDGE,"E114"),sQuery(id+"F6.wireOp",EDGE,"E161.MirrorCS"),sQuery(id+"F6.wireOp",EDGE,"E162.MirrorCS"),sQuery(id+"F6.wireOp",EDGE,"E163.MirrorCS"),sQuery(id+"F6.wireOp",EDGE,"E166"),sQuery(id+"F6.wireOp",EDGE,"E167"),sQuery(id+"F6.wireOp",EDGE,"E168"),sQuery(id+"F6.wireOp",EDGE,"E169"),sQuery(id+"F6.wireOp",EDGE,"E170"),sQuery(id+"F6.wireOp",EDGE,"E171"),sQuery(id+"F6.wireOp",EDGE,"E172"),sQuery(id+"F6.wireOp",EDGE,"E173.MirrorCS"),sQuery(id+"F6.wireOp",EDGE,"E174.MirrorCS"),sQuery(id+"F6.wireOp",EDGE,"E175.MirrorCS"),sQuery(id+"F6.wireOp",EDGE,"E176.MirrorCS"),sQuery(id+"F6.wireOp",EDGE,"E177.MirrorCS"),sQuery(id+"F6.wireOp",EDGE,"E178.MirrorCS"),sQuery(id+"F6.wireOp",EDGE,"E179.MirrorCS"),sQuery(id+"F6.wireOp",EDGE,"E180.MirrorCS"),sQuery(id+"F6.wireOp",EDGE,"E181.MirrorCS"),sQuery(id+"F6.wireOp",EDGE,"E182.MirrorCS"),sQuery(id+"F6.wireOp",EDGE,"E183.MirrorCS"),sQuery(id+"F6.wireOp",EDGE,"E184.MirrorCS"),sQuery(id+"F6.wireOp",EDGE,"E185.MirrorCS"),sQuery(id+"F6.wireOp",EDGE,"E186.MirrorCS"),sQuery(id+"F6.wireOp",EDGE,"E187.MirrorCS"),sQuery(id+"F6.wireOp",EDGE,"E188.MirrorCS"),sQuery(id+"F6.wireOp",EDGE,"E189.MirrorCS"),sQuery(id+"F6.wireOp",EDGE,"E190.MirrorCS"),sQuery(id+"F6.wireOp",EDGE,"E123.top"),sQuery(id+"F6.wireOp",EDGE,"E191.MirrorCS"),sQuery(id+"F6.wireOp",EDGE,"E192.MirrorCS"),sQuery(id+"F6.wireOp",EDGE,"E193.MirrorCS")])],"isStart":false});
            var sketch = newSketch(context, id + "F22", { "sketchPlane" : qUnion([Q0])});
            skCircle(sketch, "E248.0", {"center": v(-0.65, 16.29) * mm, "radius": 3.4 * mm});
            skCircle(sketch, "E248.1", {"center": v(-0.65, -13.71) * mm, "radius": 3.4 * mm});
            skLineSegment(sketch, "E248.2", {"start": v(-13.65, -28.71) * mm, "end": v(-4.65, -28.71) * mm});
            skLineSegment(sketch, "E248.3", {"start": v(-15.65, -17.71) * mm, "end": v(-15.65, -26.71) * mm});
            skArc(sketch, "E248.4", {"start": v(-13.65, -28.71) * mm, "mid": v(-15.07, -28.13) * mm, "end": v(-15.65, -26.71) * mm});
            skLineSegment(sketch, "E248.5", {"start": v(3.35, -28.71) * mm, "end": v(12.35, -28.71) * mm});
            skArc(sketch, "E248.6", {"start": v(12.35, -28.71) * mm, "mid": v(13.76, -28.13) * mm, "end": v(14.35, -26.71) * mm});
            skLineSegment(sketch, "E248.7", {"start": v(14.35, -17.71) * mm, "end": v(14.35, -26.71) * mm});
            skLineSegment(sketch, "E248.8", {"start": v(3.35, 31.29) * mm, "end": v(12.35, 31.29) * mm});
            skArc(sketch, "E248.9", {"start": v(12.35, 31.29) * mm, "mid": v(13.76, 30.7) * mm, "end": v(14.35, 29.29) * mm});
            skLineSegment(sketch, "E248.10", {"start": v(14.35, 29.29) * mm, "end": v(14.35, 20.29) * mm});
            skLineSegment(sketch, "E248.11", {"start": v(-15.65, 29.29) * mm, "end": v(-15.65, 20.29) * mm});
            skLineSegment(sketch, "E248.12", {"start": v(-13.65, 31.29) * mm, "end": v(-4.65, 31.29) * mm});
            skArc(sketch, "E248.13", {"start": v(-13.65, 31.29) * mm, "mid": v(-15.07, 30.7) * mm, "end": v(-15.65, 29.29) * mm});
            skLineSegment(sketch, "E249", {"start": v(-15.65, 20.29) * mm, "end": v(-15.65, -17.71) * mm});
            skLineSegment(sketch, "E250", {"start": v(-4.65, -28.71) * mm, "end": v(3.35, -28.71) * mm});
            skLineSegment(sketch, "E251", {"start": v(14.35, -17.71) * mm, "end": v(14.35, 20.29) * mm});
            skLineSegment(sketch, "E252", {"start": v(3.35, 31.29) * mm, "end": v(-4.65, 31.29) * mm});
            skSolve(sketch);
        }
        {
            var Q0;
            Q0=makeQuery(id+"F22.imprint","IMPRINT",FACE,{"disambiguationData":[TD([[makeQuery(id+"F22.imprint","IMPRINT",EDGE,{"derivedFrom":sQuery(id+"F22.wireOp",EDGE,"E248.0")}),-1.0]])]});
            var Q1;
            Q1=makeQuery(id+"F22.imprint","IMPRINT",FACE,{"disambiguationData":[TD([[makeQuery(id+"F22.imprint","IMPRINT",EDGE,{"derivedFrom":makeQuery(id+"F7.opExtrude","CAP_EDGE",EDGE,{"disambiguationData":[OSD([sQuery(id+"F6.wireOp",EDGE,"E118.right")])],"isStart":false})}),1.0]])]});
            var Q2;
            Q2=makeQuery(id+"F22.imprint","IMPRINT",FACE,{"disambiguationData":[TD([[makeQuery(id+"F22.imprint","IMPRINT",EDGE,{"derivedFrom":makeQuery(id+"F7.opExtrude","CAP_EDGE",EDGE,{"disambiguationData":[OSD([sQuery(id+"F6.wireOp",EDGE,"E123.right")])],"isStart":false})}),1.0]])]});
            var Q3;
            Q3=makeQuery(id+"F22.imprint","IMPRINT",FACE,{"disambiguationData":[TD([[makeQuery(id+"F22.imprint","IMPRINT",EDGE,{"derivedFrom":sQuery(id+"F22.wireOp",EDGE,"E250")}),1.0]])]});
            var Q4;
            Q4=makeQuery(id+"F22.imprint","IMPRINT",FACE,{"disambiguationData":[TD([[makeQuery(id+"F22.imprint","IMPRINT",EDGE,{"derivedFrom":makeQuery(id+"F7.opExtrude","CAP_EDGE",EDGE,{"disambiguationData":[OSD([sQuery(id+"F6.wireOp",EDGE,"E123.left")])],"isStart":false})}),-1.0]])]});
            var Q5;
            Q5=makeQuery(id+"F22.imprint","IMPRINT",FACE,{"disambiguationData":[TD([[makeQuery(id+"F22.imprint","IMPRINT",EDGE,{"derivedFrom":makeQuery(id+"F7.opExtrude","CAP_EDGE",EDGE,{"disambiguationData":[OSD([sQuery(id+"F6.wireOp",EDGE,"E118.left")])],"isStart":false})}),-1.0]])]});
            var Q6;
            Q6=makeQuery(id+"F22.imprint","IMPRINT",FACE,{"disambiguationData":[TD([[makeQuery(id+"F22.imprint","IMPRINT",EDGE,{"derivedFrom":sQuery(id+"F22.wireOp",EDGE,"E252")}),1.0]])]});
            var Q7;
            Q7=makeQuery(id+"F22.imprint","IMPRINT",FACE,{"disambiguationData":[TD([[makeQuery(id+"F22.imprint","IMPRINT",EDGE,{"derivedFrom":makeQuery(id+"F7.opExtrude","CAP_EDGE",EDGE,{"disambiguationData":[OSD([sQuery(id+"F6.wireOp",EDGE,"E111")])],"isStart":false})}),1.0]])]});
            var Q8;
            Q8=makeQuery(id+"F22.imprint","IMPRINT",FACE,{"disambiguationData":[TD([[makeQuery(id+"F22.imprint","IMPRINT",EDGE,{"derivedFrom":makeQuery(id+"F7.opExtrude","CAP_EDGE",EDGE,{"disambiguationData":[OSD([sQuery(id+"F6.wireOp",EDGE,"E118.bottom")])],"isStart":false})}),1.0]])]});
            var Q9;
            Q9=makeQuery(id+"F22.imprint","IMPRINT",FACE,{"disambiguationData":[TD([[makeQuery(id+"F22.imprint","IMPRINT",EDGE,{"derivedFrom":makeQuery(id+"F7.opExtrude","CAP_EDGE",EDGE,{"disambiguationData":[OSD([sQuery(id+"F6.wireOp",EDGE,"E112")])],"isStart":false})}),-1.0]])]});
            var Q10;
            Q10=makeQuery(id+"F22.imprint","IMPRINT",FACE,{"disambiguationData":[TD([[makeQuery(id+"F22.imprint","IMPRINT",EDGE,{"derivedFrom":makeQuery(id+"F7.opExtrude","CAP_EDGE",EDGE,{"disambiguationData":[OSD([sQuery(id+"F6.wireOp",EDGE,"E113")])],"isStart":false})}),1.0]])]});
            var Q11;
            Q11=makeQuery(id+"F22.imprint","IMPRINT",FACE,{"disambiguationData":[TD([[makeQuery(id+"F22.imprint","IMPRINT",EDGE,{"derivedFrom":makeQuery(id+"F7.opExtrude","CAP_EDGE",EDGE,{"disambiguationData":[OSD([sQuery(id+"F6.wireOp",EDGE,"E114")])],"isStart":false})}),-1.0]])]});
            extrude(context, id + "F23", {"entities" : qUnion([Q0, Q1, Q2, Q3, Q4, Q5, Q6, Q7, Q8, Q9, Q10, Q11]), "depth" : 6.35 * mm, "offsetDistance" : 25 * mm});
        }
        {
            var Q0;
            Q0=makeQuery(id+"F23.opExtrude","CAP_FACE",FACE,{"disambiguationData":[OSD([sQuery(id+"F22.wireOp",EDGE,"E248.0"),sQuery(id+"F22.wireOp",EDGE,"E248.1"),sQuery(id+"F22.wireOp",EDGE,"E248.2"),sQuery(id+"F22.wireOp",EDGE,"E248.3"),sQuery(id+"F22.wireOp",EDGE,"E248.4"),sQuery(id+"F22.wireOp",EDGE,"E248.5"),sQuery(id+"F22.wireOp",EDGE,"E248.6"),sQuery(id+"F22.wireOp",EDGE,"E248.7"),sQuery(id+"F22.wireOp",EDGE,"E248.8"),sQuery(id+"F22.wireOp",EDGE,"E248.9"),sQuery(id+"F22.wireOp",EDGE,"E248.10"),sQuery(id+"F22.wireOp",EDGE,"E248.11"),sQuery(id+"F22.wireOp",EDGE,"E248.12"),sQuery(id+"F22.wireOp",EDGE,"E248.13"),sQuery(id+"F22.wireOp",EDGE,"E249"),sQuery(id+"F22.wireOp",EDGE,"E250"),sQuery(id+"F22.wireOp",EDGE,"E251"),sQuery(id+"F22.wireOp",EDGE,"E252")])],"isStart":false});
            var sketch = newSketch(context, id + "F24", { "sketchPlane" : qUnion([Q0])});
            skLineSegment(sketch, "E253", {"start": v(-0.65, 31.29) * mm, "end": v(0, -28.71) * mm, "construction": true});
            skLineSegment(sketch, "E254", {"start": v(-15.65, 1.29) * mm, "end": v(14.35, 1.29) * mm, "construction": true});
            skLineSegment(sketch, "E255.bottom", {"start": v(-15.65, 7.64) * mm, "end": v(14.35, 7.64) * mm});
            skLineSegment(sketch, "E255.left", {"start": v(-15.65, 7.64) * mm, "end": v(-15.65, 1.29) * mm});
            skLineSegment(sketch, "E255.right", {"start": v(14.35, 7.64) * mm, "end": v(14.35, 1.29) * mm});
            skLineSegment(sketch, "E256.MirrorCS", {"start": v(-15.65, -5.06) * mm, "end": v(-15.65, 1.29) * mm});
            skLineSegment(sketch, "E257.MirrorCS", {"start": v(-15.65, -5.06) * mm, "end": v(14.35, -5.06) * mm});
            skLineSegment(sketch, "E258.MirrorCS", {"start": v(14.35, -5.06) * mm, "end": v(14.35, 1.29) * mm});
            skSolve(sketch);
        }
        {
            var Q0;
            Q0=makeQuery(id+"F24.imprint","IMPRINT",FACE,{"disambiguationData":[TD([[makeQuery(id+"F24.imprint","IMPRINT",EDGE,{"derivedFrom":sQuery(id+"F24.wireOp",EDGE,"E255.bottom")}),-1.0]])]});
            extrude(context, id + "F25", {"entities" : qUnion([Q0]), "depth" : 25 * mm, "offsetDistance" : 25 * mm});
        }
        {
            var Q0;
            Q0=makeQuery(id+"F25.opExtrude","SWEPT_FACE",FACE,{"disambiguationData":[OSD([sQuery(id+"F24.wireOp",EDGE,"E255.bottom")])]});
            var sketch = newSketch(context, id + "F26", { "sketchPlane" : qUnion([Q0])});
            skLineSegment(sketch, "E259", {"start": v(-14.35, 118.85) * mm, "end": v(15.65, 118.85) * mm, "construction": true});
            skCircle(sketch, "E260", {"center": v(0.65, 118.85) * mm, "radius": 6.35 * mm});
            skSolve(sketch);
        }
        {
            var Q0;
            Q0=makeQuery(id+"F26.imprint","IMPRINT",FACE,{"disambiguationData":[TD([[makeQuery(id+"F26.imprint","IMPRINT",EDGE,{"derivedFrom":sQuery(id+"F26.wireOp",EDGE,"E260")}),1.0]])]});
            extrude(context, id + "F27", {"entities" : qUnion([Q0]), "operationType" : NewBodyOperationType.REMOVE, "endBound" : BoundingType.THROUGH_ALL, "oppositeDirection" : true, "depth" : 25 * mm, "offsetDistance" : 25 * mm});
        }
    });
